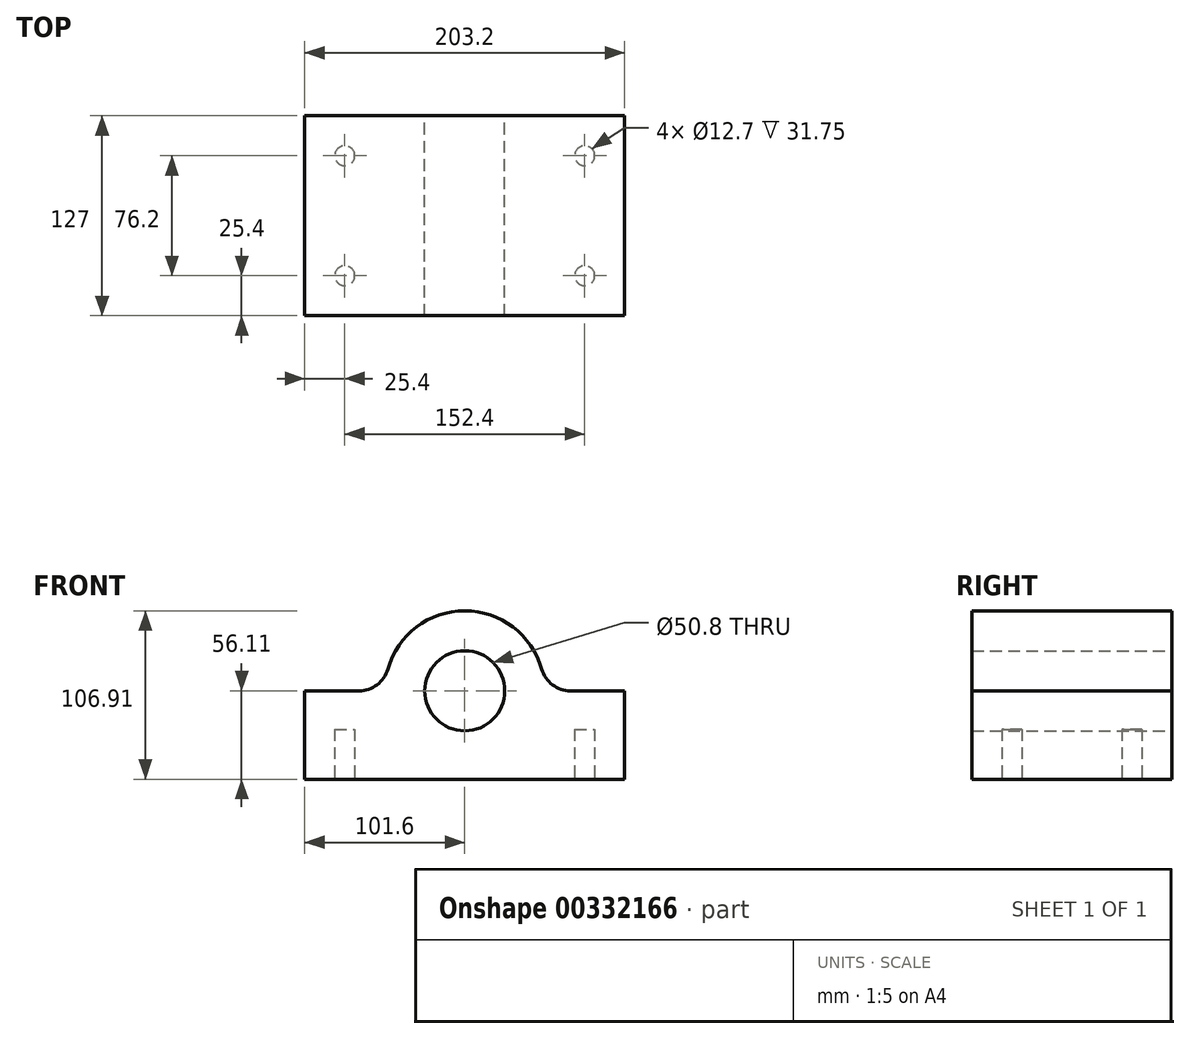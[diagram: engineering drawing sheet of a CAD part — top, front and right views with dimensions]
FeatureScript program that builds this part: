
annotation { "Feature Type Name" : "Feature", "Feature Type Description" : "" }
export const myFeature = defineFeature(function(context is Context, id is Id, definition is map)
    precondition{}
    {
        {
            var Q0;
            Q0=qCreatedBy(makeId("Front.planeOp"),FACE);
            var sketch = newSketch(context, id + "F0", { "sketchPlane" : qUnion([Q0])});
            skCircle(sketch, "E0", {"center": v(0, 0) * mm, "radius": 25.38 * mm});
            skCircle(sketch, "E1", {"center": v(0, 0) * mm, "radius": 25.4 * mm});
            skLineSegment(sketch, "E2.trimOffspring", {"start": v(-25.4, 0) * mm, "end": v(-25.38, 0) * mm});
            skLineSegment(sketch, "E3.trimOffspring", {"start": v(25.38, 0) * mm, "end": v(25.4, 0) * mm});
            skLineSegment(sketch, "E4", {"start": v(0, -25.38) * mm, "end": v(0, -25.4) * mm});
            skLineSegment(sketch, "E5", {"start": v(0, -56.1) * mm, "end": v(-101.6, -56.1) * mm});
            skLineSegment(sketch, "E6", {"start": v(0, -56.1) * mm, "end": v(101.6, -56.1) * mm});
            skLineSegment(sketch, "E7", {"start": v(-101.6, -56.1) * mm, "end": v(-101.6, 0) * mm});
            skLineSegment(sketch, "E8", {"start": v(101.6, -56.1) * mm, "end": v(101.6, 0) * mm});
            skLineSegment(sketch, "E9", {"start": v(101.6, 0) * mm, "end": v(67.2, 0) * mm});
            skArc(sketch, "E10", {"start": v(48.87, 13.85) * mm, "mid": v(0, 50.8) * mm, "end": v(-48.87, 13.85) * mm});
            skArc(sketch, "E11", {"start": v(-67.2, 0) * mm, "mid": v(-55.71, 3.85) * mm, "end": v(-48.87, 13.85) * mm});
            skArc(sketch, "E12", {"start": v(48.87, 13.85) * mm, "mid": v(55.71, 3.85) * mm, "end": v(67.2, 0) * mm});
            skLineSegment(sketch, "E13.trimOffspring", {"start": v(-25.38, 0) * mm, "end": v(-25.4, 0) * mm});
            skLineSegment(sketch, "E14.trimOffspring", {"start": v(25.4, 0) * mm, "end": v(25.38, 0) * mm});
            skLineSegment(sketch, "E15.trimOffspring", {"start": v(-67.2, 0) * mm, "end": v(-101.6, 0) * mm});
            skSolve(sketch);
        }
        {
            var Q0;
            Q0 = qSketchRegion(id + "F0", true);
            extrude(context, id + "F1", {"entities" : qUnion([Q0]), "depth" : 127 * mm});
        }
        {
            var Q0;
            Q0=makeQuery(id+"F1.opExtrude","SWEPT_FACE",FACE,{"disambiguationData":[OSD([sQuery(id+"F0.wireOp",EDGE,"E5"),sQuery(id+"F0.wireOp",EDGE,"E6")])]});
            var sketch = newSketch(context, id + "F2", { "sketchPlane" : qUnion([Q0])});
            skCircle(sketch, "E16", {"center": v(-76.2, 101.6) * mm, "radius": 6.35 * mm});
            skCircle(sketch, "E17", {"center": v(-76.2, 25.4) * mm, "radius": 6.35 * mm});
            skCircle(sketch, "E18", {"center": v(76.2, 101.6) * mm, "radius": 6.35 * mm});
            skCircle(sketch, "E19", {"center": v(76.2, 25.4) * mm, "radius": 6.35 * mm});
            skSolve(sketch);
        }
        {
            var Q0;
            Q0=makeQuery(id+"F2.imprint","IMPRINT",FACE,{"disambiguationData":[TD([[makeQuery(id+"F2.imprint","IMPRINT",EDGE,{"derivedFrom":sQuery(id+"F2.wireOp",EDGE,"E16")}),1.0]])]});
            var Q1;
            Q1=makeQuery(id+"F2.imprint","IMPRINT",FACE,{"disambiguationData":[TD([[makeQuery(id+"F2.imprint","IMPRINT",EDGE,{"derivedFrom":sQuery(id+"F2.wireOp",EDGE,"E17")}),1.0]])]});
            var Q2;
            Q2=makeQuery(id+"F2.imprint","IMPRINT",FACE,{"disambiguationData":[TD([[makeQuery(id+"F2.imprint","IMPRINT",EDGE,{"derivedFrom":sQuery(id+"F2.wireOp",EDGE,"E18")}),1.0]])]});
            var Q3;
            Q3=makeQuery(id+"F2.imprint","IMPRINT",FACE,{"disambiguationData":[TD([[makeQuery(id+"F2.imprint","IMPRINT",EDGE,{"derivedFrom":sQuery(id+"F2.wireOp",EDGE,"E19")}),1.0]])]});
            extrude(context, id + "F3", {"entities" : qUnion([Q0, Q1, Q2, Q3]), "operationType" : NewBodyOperationType.REMOVE, "oppositeDirection" : true, "depth" : 31.75 * mm});
        }
    });
